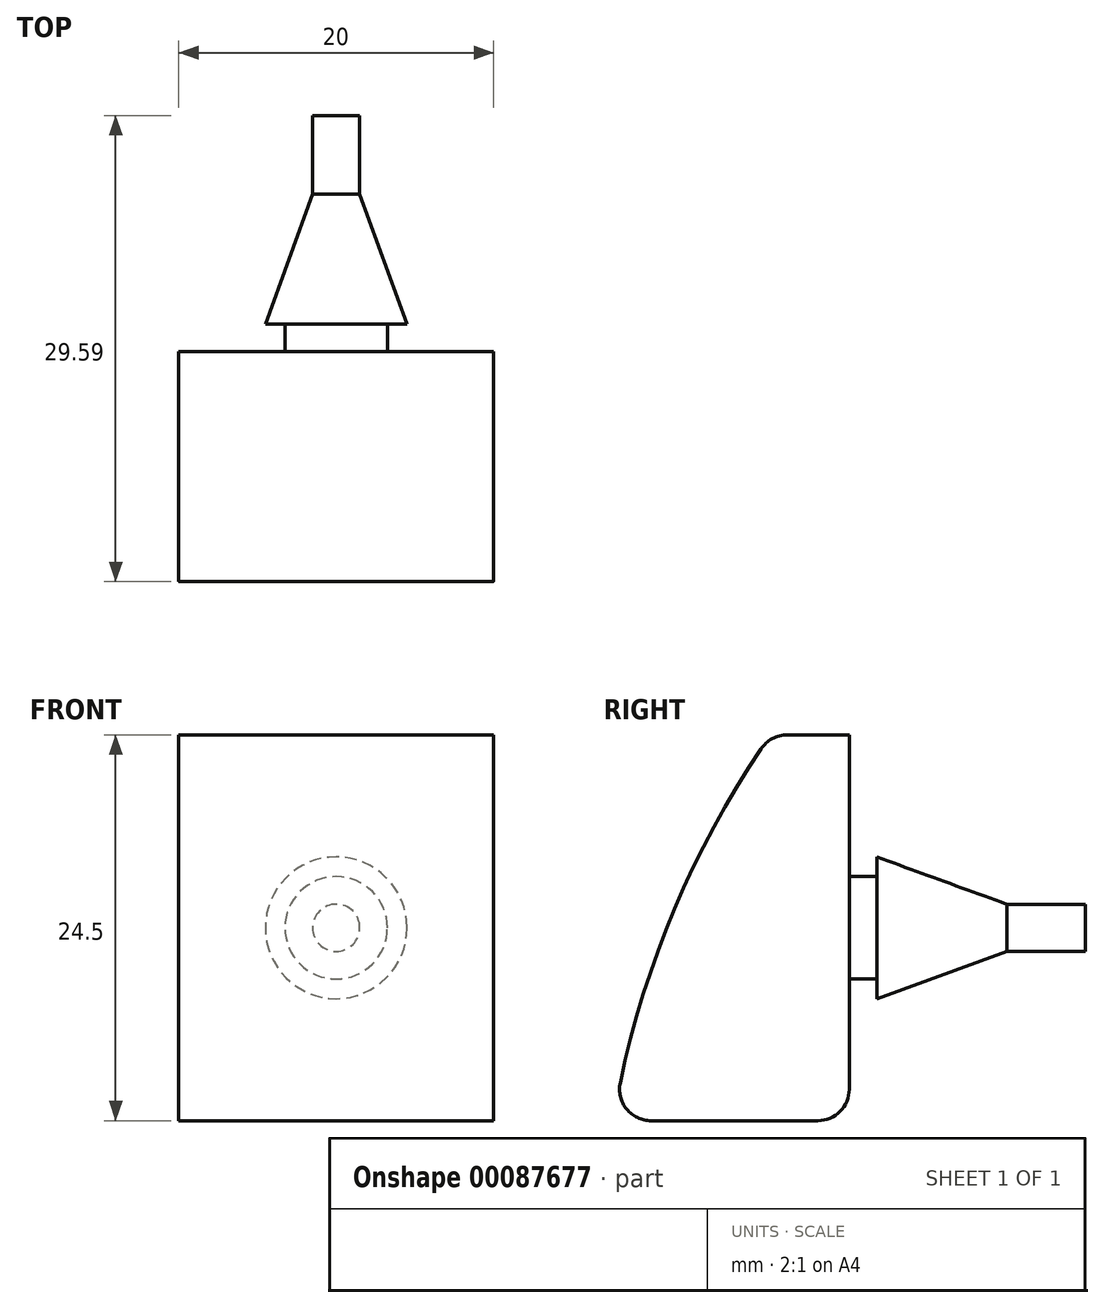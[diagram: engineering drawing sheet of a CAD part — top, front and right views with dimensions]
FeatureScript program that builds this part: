
annotation { "Feature Type Name" : "Feature", "Feature Type Description" : "" }
export const myFeature = defineFeature(function(context is Context, id is Id, definition is map)
    precondition{}
    {
        {
            var Q0;
            Q0=qCreatedBy(makeId("Right.planeOp"),FACE);
            var sketch = newSketch(context, id + "F0", { "sketchPlane" : qUnion([Q0])});
            skPoint(sketch, "E0.middle", {"position": v(0, 0) * mm});
            skLineSegment(sketch, "E1", {"start": v(0, 0) * mm, "end": v(-15, 0) * mm});
            skLineSegment(sketch, "E2", {"start": v(0, 0) * mm, "end": v(0, 24.5) * mm});
            skLineSegment(sketch, "E3", {"start": v(0, 24.5) * mm, "end": v(-5, 24.5) * mm});
            skArc(sketch, "E4", {"start": v(-5, 24.5) * mm, "mid": v(-11.37, 12.8) * mm, "end": v(-15, 0) * mm});
            skPoint(sketch, "E4.third.point", {"position": v(95.24, 21.65) * mm});
            skSolve(sketch);
        }
        {
            var Q0;
            Q0 = qSketchRegion(id + "F0", true);
            extrude(context, id + "F1", {"entities" : qUnion([Q0]), "endBound" : BoundingType.SYMMETRIC, "depth" : 20 * mm});
        }
        {
            var Q0;
            Q0=makeQuery(id+"F1.opExtrude","SWEPT_FACE",FACE,{"disambiguationData":[OSD([sQuery(id+"F0.wireOp",EDGE,"E2")])]});
            var sketch = newSketch(context, id + "F2", { "sketchPlane" : qUnion([Q0])});
            skPoint(sketch, "E5", {"position": v(0, 12.25) * mm});
            skPoint(sketch, "E5.positionSnap0", {"position": v(-10, 12.25) * mm});
            skPoint(sketch, "E5.positionSnap1", {"position": v(0, 24.5) * mm});
            skSolve(sketch);
        }
        {
            var Q0;
            Q0=qCreatedBy(makeId("Right.planeOp"),FACE);
            var sketch = newSketch(context, id + "F3", { "sketchPlane" : qUnion([Q0])});
            skLineSegment(sketch, "E6", {"start": v(15, 12.25) * mm, "end": v(0, 12.25) * mm});
            skLineSegment(sketch, "E7", {"start": v(0, 15.5) * mm, "end": v(1.75, 15.5) * mm});
            skLineSegment(sketch, "E8", {"start": v(1.75, 15.5) * mm, "end": v(1.75, 16.75) * mm});
            skLineSegment(sketch, "E9", {"start": v(1.75, 16.75) * mm, "end": v(10, 13.75) * mm});
            skLineSegment(sketch, "E10", {"start": v(10, 13.75) * mm, "end": v(15, 13.75) * mm});
            skLineSegment(sketch, "E11", {"start": v(0, 15.5) * mm, "end": v(0, 12.25) * mm});
            skLineSegment(sketch, "E12", {"start": v(15, 13.75) * mm, "end": v(15, 12.25) * mm});
            skSolve(sketch);
        }
        {
            var Q0;
            Q0=makeQuery(id+"F3.imprint","IMPRINT",FACE,{"disambiguationData":[TD([[makeQuery(id+"F3.imprint","IMPRINT",EDGE,{"derivedFrom":sQuery(id+"F3.wireOp",EDGE,"E6")}),-1.0]])]});
            var Q1;
            Q1=sQuery(id+"F3.wireOp",EDGE,"E6");
            revolve(context, id + "F4", {"operationType" : NewBodyOperationType.ADD, "entities" : qUnion([Q0]), "axis" : qUnion([Q1]), "revolveType" : RevolveType.FULL});
        }
        {
            var Q0;
            Q0=makeQuery(id+"F1.opExtrude","SWEPT_EDGE",EDGE,{"disambiguationData":[OSD([sQuery(id+"F0.wireOp",EDGE,"E3"),sQuery(id+"F0.wireOp",EDGE,"E4")])]});
            var Q1;
            Q1=makeQuery(id+"F1.opExtrude","SWEPT_EDGE",EDGE,{"disambiguationData":[OSD([sQuery(id+"F0.wireOp",EDGE,"E1"),sQuery(id+"F0.wireOp",EDGE,"E4")])]});
            var Q2;
            Q2=makeQuery(id+"F1.opExtrude","SWEPT_EDGE",EDGE,{"disambiguationData":[OSD([sQuery(id+"F0.wireOp",EDGE,"E1"),sQuery(id+"F0.wireOp",EDGE,"E2")])]});
            fillet(context, id + "F5", {"entities" : qUnion([Q0, Q1, Q2]), "radius" : 2 * mm, "tangentPropagation" : true, "allowEdgeOverflow" : false});
        }
    });
